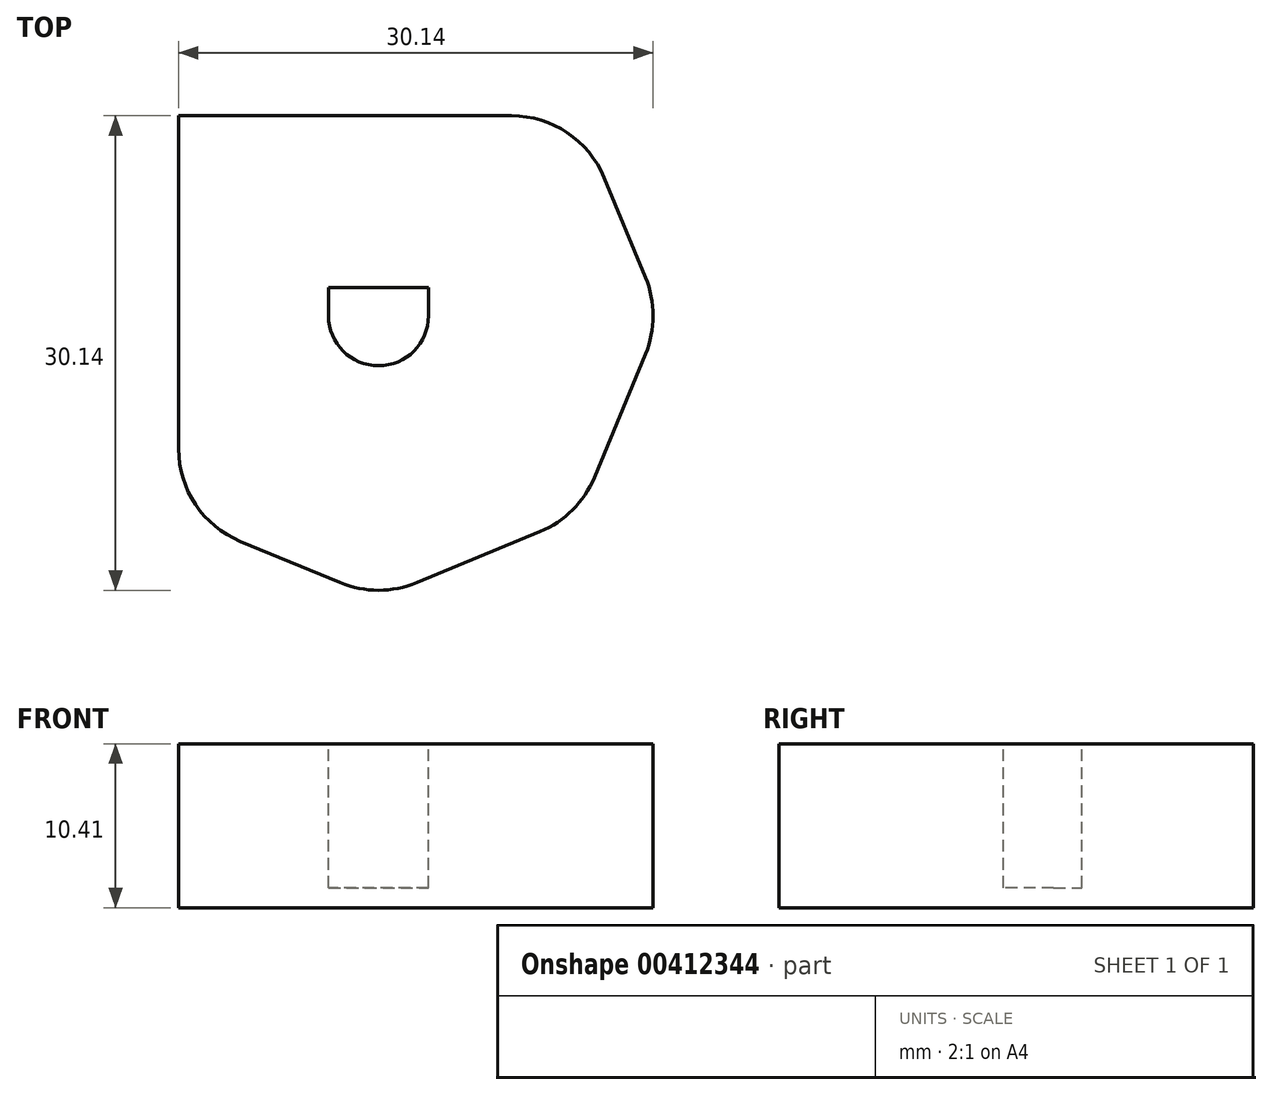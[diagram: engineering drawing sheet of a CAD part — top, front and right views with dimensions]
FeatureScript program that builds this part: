
annotation { "Feature Type Name" : "Feature", "Feature Type Description" : "" }
export const myFeature = defineFeature(function(context is Context, id is Id, definition is map)
    precondition{}
    {
        {
            var Q0;
            Q0=qCreatedBy(makeId("Top.planeOp"),FACE);
            var sketch = newSketch(context, id + "F0", { "sketchPlane" : qUnion([Q0])});
            skArc(sketch, "E0", {"start": v(3.18, 0) * mm, "mid": v(0, 3.18) * mm, "end": v(-3.18, 0) * mm});
            skLineSegment(sketch, "E1", {"start": v(3.18, 0) * mm, "end": v(3.18, -1.78) * mm});
            skLineSegment(sketch, "E2", {"start": v(-3.18, 0) * mm, "end": v(-3.18, -1.78) * mm});
            skLineSegment(sketch, "E3", {"start": v(-3.18, -1.78) * mm, "end": v(3.18, -1.78) * mm});
            skCircle(sketch, "E4.cCircle", {"center": v(0, 0) * mm, "radius": 17.96 * mm, "construction": true});
            skLineSegment(sketch, "E4.4", {"start": v(-12.7, 12.7) * mm, "end": v(0, 17.96) * mm});
            skLineSegment(sketch, "E4.5", {"start": v(0, 17.96) * mm, "end": v(12.7, 12.7) * mm});
            skLineSegment(sketch, "E4.6", {"start": v(12.7, 12.7) * mm, "end": v(17.96, 0) * mm});
            skLineSegment(sketch, "E4.7", {"start": v(17.96, 0) * mm, "end": v(12.7, -12.7) * mm});
            skLineSegment(sketch, "E5", {"start": v(12.7, -12.7) * mm, "end": v(-12.7, -12.7) * mm});
            skLineSegment(sketch, "E6", {"start": v(-12.7, 12.7) * mm, "end": v(-12.7, -12.7) * mm});
            skSolve(sketch);
        }
        {
            var Q0;
            Q0=makeQuery(id+"F0.imprint","IMPRINT",FACE,{"disambiguationData":[TD([[makeQuery(id+"F0.imprint","IMPRINT",EDGE,{"derivedFrom":sQuery(id+"F0.wireOp",EDGE,"E0")}),-1.0]])]});
            extrude(context, id + "F1", {"entities" : qUnion([Q0]), "depth" : 10.4 * mm});
        }
        {
            var Q0;
            Q0=makeQuery(id+"F1.opExtrude","CAP_FACE",FACE,{"disambiguationData":[OSD([sQuery(id+"F0.wireOp",EDGE,"E0"),sQuery(id+"F0.wireOp",EDGE,"E1"),sQuery(id+"F0.wireOp",EDGE,"E2"),sQuery(id+"F0.wireOp",EDGE,"E3"),sQuery(id+"F0.wireOp",EDGE,"E4.4"),sQuery(id+"F0.wireOp",EDGE,"E4.5"),sQuery(id+"F0.wireOp",EDGE,"E4.6"),sQuery(id+"F0.wireOp",EDGE,"E4.7"),sQuery(id+"F0.wireOp",EDGE,"E5"),sQuery(id+"F0.wireOp",EDGE,"E6")])],"isStart":false});
            var sketch = newSketch(context, id + "F2", { "sketchPlane" : qUnion([Q0])});
            skLineSegment(sketch, "E7", {"start": v(-3.18, 0) * mm, "end": v(-3.18, -1.78) * mm});
            skLineSegment(sketch, "E8", {"start": v(-3.18, -1.78) * mm, "end": v(3.18, -1.78) * mm});
            skLineSegment(sketch, "E9", {"start": v(3.18, -1.78) * mm, "end": v(3.18, 0) * mm});
            skArc(sketch, "E10", {"start": v(3.17, 0) * mm, "mid": v(0, 3.18) * mm, "end": v(-3.18, 0) * mm});
            skSolve(sketch);
        }
        {
            var Q0;
            Q0 = qSketchRegion(id + "F2", true);
            extrude(context, id + "F3", {"entities" : qUnion([Q0]), "operationType" : NewBodyOperationType.ADD, "oppositeDirection" : true, "depth" : 1.27 * mm});
        }
        {
            var Q0;
            Q0=makeQuery(id+"F1.opExtrude","SWEPT_EDGE",EDGE,{"disambiguationData":[OSD([sQuery(id+"F0.wireOp",EDGE,"E4.7"),sQuery(id+"F0.wireOp",EDGE,"E5")])]});
            var Q1;
            Q1=makeQuery(id+"F1.opExtrude","SWEPT_EDGE",EDGE,{"disambiguationData":[OSD([sQuery(id+"F0.wireOp",EDGE,"E4.6"),sQuery(id+"F0.wireOp",EDGE,"E4.7")])]});
            var Q2;
            Q2=makeQuery(id+"F1.opExtrude","SWEPT_EDGE",EDGE,{"disambiguationData":[OSD([sQuery(id+"F0.wireOp",EDGE,"E4.5"),sQuery(id+"F0.wireOp",EDGE,"E4.6")])]});
            var Q3;
            Q3=makeQuery(id+"F1.opExtrude","SWEPT_EDGE",EDGE,{"disambiguationData":[OSD([sQuery(id+"F0.wireOp",EDGE,"E4.4"),sQuery(id+"F0.wireOp",EDGE,"E4.5")])]});
            var Q4;
            Q4=makeQuery(id+"F1.opExtrude","SWEPT_EDGE",EDGE,{"disambiguationData":[OSD([sQuery(id+"F0.wireOp",EDGE,"E4.4"),sQuery(id+"F0.wireOp",EDGE,"E6")])]});
            fillet(context, id + "F4", {"entities" : qUnion([Q0, Q1, Q2, Q3, Q4]), "radius" : 6.35 * mm, "tangentPropagation" : true, "allowEdgeOverflow" : false});
        }
        {
            var Q0;
            Q0=qCreatedBy(makeId("Top.planeOp"),FACE);
            var sketch = newSketch(context, id + "F5", { "sketchPlane" : qUnion([Q0])});
            skLineSegment(sketch, "E11", {"start": v(0, 0) * mm, "end": v(21.42, 0) * mm});
            skSolve(sketch);
        }
        {
            var Q0;
            Q0=makeQuery(id+"F1.opExtrude","SWEPT_BODY",BODY,{"disambiguationData":[OSD([sQuery(id+"F0.wireOp",EDGE,"E0"),sQuery(id+"F0.wireOp",EDGE,"E1"),sQuery(id+"F0.wireOp",EDGE,"E2"),sQuery(id+"F0.wireOp",EDGE,"E3"),sQuery(id+"F0.wireOp",EDGE,"E4.4"),sQuery(id+"F0.wireOp",EDGE,"E4.5"),sQuery(id+"F0.wireOp",EDGE,"E4.6"),sQuery(id+"F0.wireOp",EDGE,"E4.7"),sQuery(id+"F0.wireOp",EDGE,"E5"),sQuery(id+"F0.wireOp",EDGE,"E6")])]});
            var Q1;
            Q1=sQuery(id+"F5.wireOp",EDGE,"E11");
            transform(context, id + "F6", {"entities" : qUnion([Q0]), "transformType" : TransformType.ROTATION, "transformAxis" : qUnion([Q1]), "angle" : 180 * degree, "makeCopy" : false});
        }
    });
